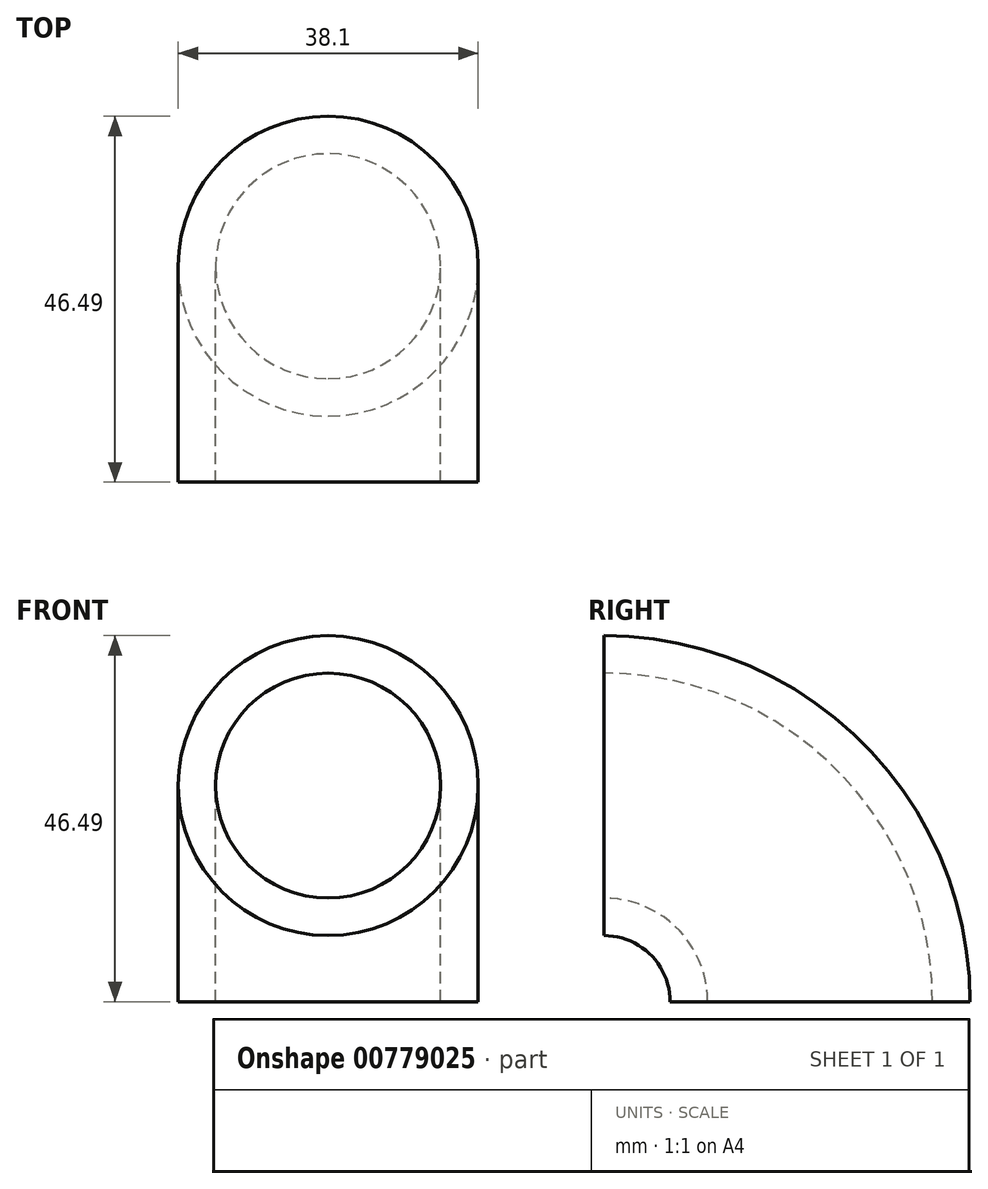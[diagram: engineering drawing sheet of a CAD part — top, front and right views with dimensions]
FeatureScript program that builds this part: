
annotation { "Feature Type Name" : "Feature", "Feature Type Description" : "" }
export const myFeature = defineFeature(function(context is Context, id is Id, definition is map)
    precondition{}
    {
        {
            var Q0;
            Q0=qCreatedBy(makeId("Front.planeOp"),FACE);
            var sketch = newSketch(context, id + "F0", { "sketchPlane" : qUnion([Q0])});
            skCircle(sketch, "E0", {"center": v(0, 0) * mm, "radius": 19.05 * mm});
            skCircle(sketch, "E1", {"center": v(0, 0) * mm, "radius": 14.29 * mm});
            skLineSegment(sketch, "E2", {"start": v(-34.05, -27.44) * mm, "end": v(35.23, -27.44) * mm});
            skSolve(sketch);
        }
        {
            var Q0;
            Q0 = qSketchRegion(id + "F0", true);
            var Q1;
            Q1=sQuery(id+"F0.wireOp",EDGE,"E2");
            revolve(context, id + "F1", {"surfaceOperationType" : NewSurfaceOperationType.NEW, "entities" : qUnion([Q0]), "axis" : qUnion([Q1]), "revolveType" : RevolveType.ONE_DIRECTION, "oppositeDirection" : true, "angle" : 90 * degree});
        }
    });
